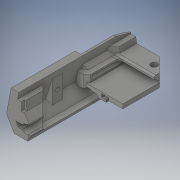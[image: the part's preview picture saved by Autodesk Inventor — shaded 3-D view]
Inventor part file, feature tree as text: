
AUTODESK INVENTOR PART (.ipt)
format: ipt  version: 2017 (Build 210142000, 142)  size: 373,248 bytes
history: native  units: in
note: dims shown in document units (in); Inventor stores cm internally (conversion verified against a paired STEP export)
features: extrude x4, sketch x4, other x2, projected_geometry x1
ambient origin geometry x8: Origin, YZ Plane, XZ Plane, XY Plane, X Axis, Y Axis, Z Axis, Center Point
bodies: Solid1 (feature_tree)
feature tree (11):
  other  "05_cache cote carte SD+Ecran.STEP"
  extrude  "Extrusion1"  Depth=0.1969in TaperAngle=0.0deg
  extrude  "Extrusion2"  Depth=0.1969in TaperAngle=0.0deg
  extrude  "Extrusion3"  [1 undecoded]
  extrude  "Extrusion4"  [1 undecoded]
  sketch  "Sketch1"  dims[d0=0.1969in d1=0.0in d2=0.1969in d3=0.0in]
  sketch  "Sketch2"  dims[d4=0.1969in d5=0.0in d6=0.1969in d7=0.0in]
  sketch  "Sketch3"
  projected_geometry  "Projected Loop1"
  sketch  "Sketch4"
  other  "Enlèv. mat.-Extru.42"
note: 2 required parameter values undecoded (feature->parameter linkage not recoverable at this tier; creation-order binding heuristic only, values carry confidence <= 0.55)
